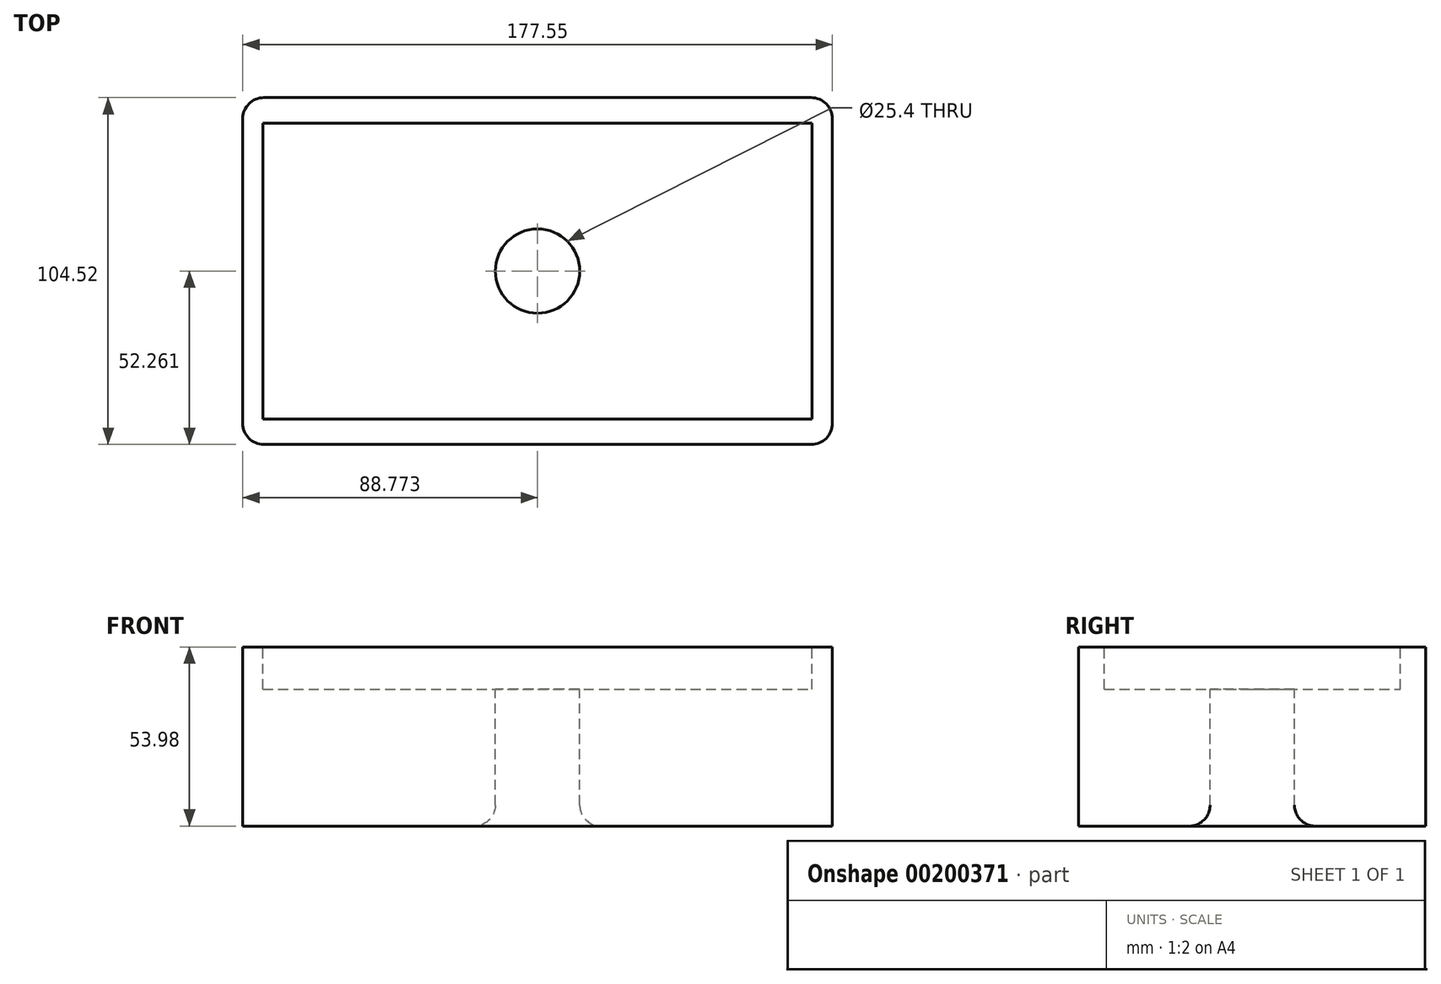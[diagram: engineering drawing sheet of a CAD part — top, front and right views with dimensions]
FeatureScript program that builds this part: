
annotation { "Feature Type Name" : "Feature", "Feature Type Description" : "" }
export const myFeature = defineFeature(function(context is Context, id is Id, definition is map)
    precondition{}
    {
        {
            var Q0;
            Q0=qCreatedBy(makeId("Top.planeOp"),FACE);
            var sketch = newSketch(context, id + "F0", { "sketchPlane" : qUnion([Q0])});
            skLineSegment(sketch, "E0.bottom", {"start": v(0, 0) * mm, "end": v(177.55, 0) * mm});
            skLineSegment(sketch, "E0.top", {"start": v(0, 104.52) * mm, "end": v(177.55, 104.52) * mm});
            skLineSegment(sketch, "E0.left", {"start": v(0, 0) * mm, "end": v(0, 104.52) * mm});
            skLineSegment(sketch, "E0.right", {"start": v(177.55, 0) * mm, "end": v(177.55, 104.52) * mm});
            skLineSegment(sketch, "E1.bottom", {"start": v(6.1, 7.68) * mm, "end": v(171.45, 7.68) * mm});
            skLineSegment(sketch, "E1.top", {"start": v(6.1, 96.84) * mm, "end": v(171.45, 96.84) * mm});
            skLineSegment(sketch, "E1.left", {"start": v(6.1, 7.68) * mm, "end": v(6.1, 96.84) * mm});
            skLineSegment(sketch, "E1.right", {"start": v(171.45, 7.68) * mm, "end": v(171.45, 96.84) * mm});
            skPoint(sketch, "E2", {"position": v(88.77, 0) * mm});
            skPoint(sketch, "E3", {"position": v(0, 52.26) * mm});
            skPoint(sketch, "E4", {"position": v(88.77, 7.68) * mm});
            skCircle(sketch, "E5", {"center": v(88.77, 52.26) * mm, "radius": 12.7 * mm});
            skPoint(sketch, "E5.centerSnap0", {"position": v(88.77, 96.84) * mm});
            skPoint(sketch, "E5.centerSnap1", {"position": v(6.1, 52.26) * mm});
            skSolve(sketch);
        }
        {
            var Q0;
            Q0=makeQuery(id+"F0.imprint","IMPRINT",FACE,{"disambiguationData":[TD([[makeQuery(id+"F0.imprint","IMPRINT",EDGE,{"derivedFrom":sQuery(id+"F0.wireOp",EDGE,"E0.bottom")}),1.0]])]});
            var Q1;
            Q1=makeQuery(id+"F0.imprint","IMPRINT",FACE,{"disambiguationData":[TD([[makeQuery(id+"F0.imprint","IMPRINT",EDGE,{"derivedFrom":sQuery(id+"F0.wireOp",EDGE,"E1.bottom")}),1.0]])]});
            extrude(context, id + "F1", {"entities" : qUnion([Q0, Q1]), "oppositeDirection" : true, "depth" : 53.97 * mm});
        }
        {
            var Q0;
            Q0=makeQuery(id+"F0.imprint","IMPRINT",FACE,{"disambiguationData":[TD([[makeQuery(id+"F0.imprint","IMPRINT",EDGE,{"derivedFrom":sQuery(id+"F0.wireOp",EDGE,"E1.bottom")}),1.0]])]});
            extrude(context, id + "F2", {"entities" : qUnion([Q0]), "operationType" : NewBodyOperationType.REMOVE, "oppositeDirection" : true, "depth" : 12.7 * mm});
        }
        {
            var Q0;
            Q0=makeQuery(id+"F1.opExtrude","SWEPT_EDGE",EDGE,{"disambiguationData":[OSD([sQuery(id+"F0.wireOp",EDGE,"E0.bottom"),sQuery(id+"F0.wireOp",EDGE,"E0.left")])]});
            var Q1;
            Q1=makeQuery(id+"F1.opExtrude","SWEPT_EDGE",EDGE,{"disambiguationData":[OSD([sQuery(id+"F0.wireOp",EDGE,"E0.top"),sQuery(id+"F0.wireOp",EDGE,"E0.right")])]});
            var Q2;
            Q2=makeQuery(id+"F1.opExtrude","SWEPT_EDGE",EDGE,{"disambiguationData":[OSD([sQuery(id+"F0.wireOp",EDGE,"E0.bottom"),sQuery(id+"F0.wireOp",EDGE,"E0.right")])]});
            var Q3;
            Q3=makeQuery(id+"F1.opExtrude","SWEPT_EDGE",EDGE,{"disambiguationData":[OSD([sQuery(id+"F0.wireOp",EDGE,"E0.top"),sQuery(id+"F0.wireOp",EDGE,"E0.left")])]});
            var Q4;
            Q4=makeQuery(id+"F2.boolean.opBoolean","COPY",EDGE,{"derivedFrom":makeQuery(id+"F2.opExtrude","CAP_EDGE",EDGE,{"disambiguationData":[OSD([sQuery(id+"F0.wireOp",EDGE,"E5")])],"isStart":false})});
            var Q5;
            Q5=makeQuery(id+"F1.opExtrude","CAP_EDGE",EDGE,{"disambiguationData":[OSD([sQuery(id+"F0.wireOp",EDGE,"E5")])],"isStart":false});
            fillet(context, id + "F3", {"entities" : qUnion([Q0, Q1, Q2, Q3, Q4, Q5]), "radius" : 6.35 * mm, "tangentPropagation" : true, "allowEdgeOverflow" : false});
        }
    });
